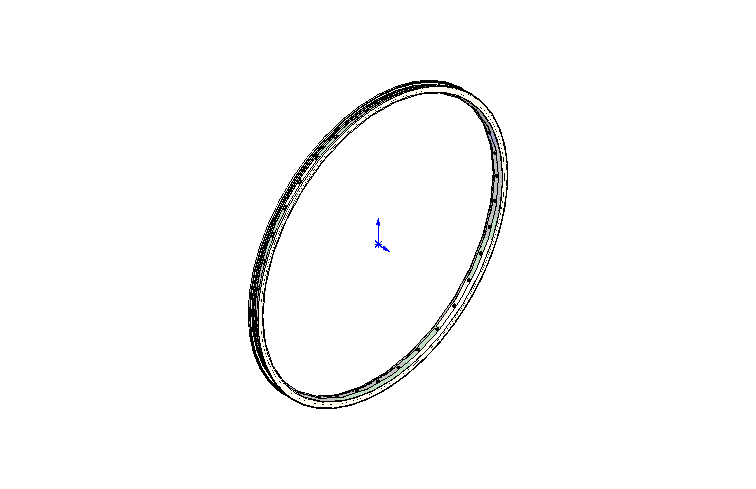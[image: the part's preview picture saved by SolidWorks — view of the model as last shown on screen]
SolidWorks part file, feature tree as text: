
SOLIDWORKS PART (.sldprt)
format: sldprt  version: not decoded by parser v0  size: 2,609,152 bytes
history: native  units: mm
features: plane x4, sketch x3, material x1, revolve x1, fillet x1, cut_revolve x1, pattern_circular x1, cut_extrude x1 (+10 scaffold rows collapsed)
feature tree (23):
  scaffold x10  (default folders/planes/origin — collapsed)
  material  "Matériau <non spécifié>"
  plane  "Plan de face"
  plane  "Plan de dessus"
  plane  "Plan de droite"
  sketch  "Esquisse1"  dims[c1.D11=1.5mm c1.D13=1.5mm c1.D14=~1.370402mm c1.D1=24.0mm c1.D2=10.0mm c1.D3=12.5mm c1.D4=600.0mm c1.D5=9.5mm c1.D6=3.5mm c1.D7=10.0mm c1.D8=3.0mm c1.D10=3.0mm c2.D5=619.0mm c2.D11=635.0mm c2.D12=0.5mm c2.D13=3.0mm c2.D14=1.0mm c2.D15=1.0mm c2.D9=1.0mm]
  revolve  "Révolution1"  Angle=360deg
  fillet  "Congé1"  Radius=0.5mm
  sketch  "Esquisse2"  dims[D1=9.0mm D2=6.5mm]
  cut_revolve  "Enlèvement de matière-Révolution1"  Angle=360deg
  pattern_circular  "Répétition circulaire1"  Count=36 Angle=10deg
  plane  "Plan1"
  sketch  "Esquisse3"  dims[D1=9.0mm]
  cut_extrude  "Enlèv. mat.-Extru.1"  [1 undecoded]
decode coverage: 7 of 8 modeling features carry decoded parameters
note: ~ marks probable driven/reference dimensions
note: 1 parameter value undecoded
note: suppression state not decoded; provenance and decode notes live in map.json
